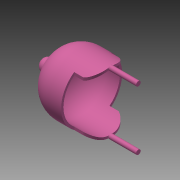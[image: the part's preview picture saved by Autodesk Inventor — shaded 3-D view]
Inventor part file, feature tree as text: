
AUTODESK INVENTOR PART (.ipt)
format: ipt  version: 2015 SP1 (Build 190203100, 203)  size: 200,704 bytes
history: native  units: in
note: dims shown in document units (in); Inventor stores cm internally (conversion verified against a paired STEP export)
features: sketch x3, extrude x2, revolve x1
ambient origin geometry x8: Origin, YZ Plane, XZ Plane, XY Plane, X Axis, Y Axis, Z Axis, Center Point
bodies: Solid1 (feature_tree)
feature tree (6):
  revolve  "Revolution1"  [1 undecoded]
  extrude  "Extrusion1"  Depth=0.25in
  extrude  "Extrusion2"  TaperAngle=90.0deg  [1 undecoded]
  sketch  "Sketch1"  dims[d0=0.5in d4=6.0in]
  sketch  "Sketch3"  dims[d5=3.05in d6=0.25in]
  sketch  "Sketch4"  dims[d7=0.5in d8=90.0deg d9=1.5in d14=1.0in d15=1.0in d18=1.3688in d22=2.0954in d23=1.4126in d24=1.0in d25=0.0in d26=0.75in d27=0.05in d28=0.5in d30=3.2001in d31=0.5in d32=3.2in d33=3.0in d34=0.0in]
note: 2 required parameter values undecoded (feature->parameter linkage not recoverable at this tier; creation-order binding heuristic only, values carry confidence <= 0.55)